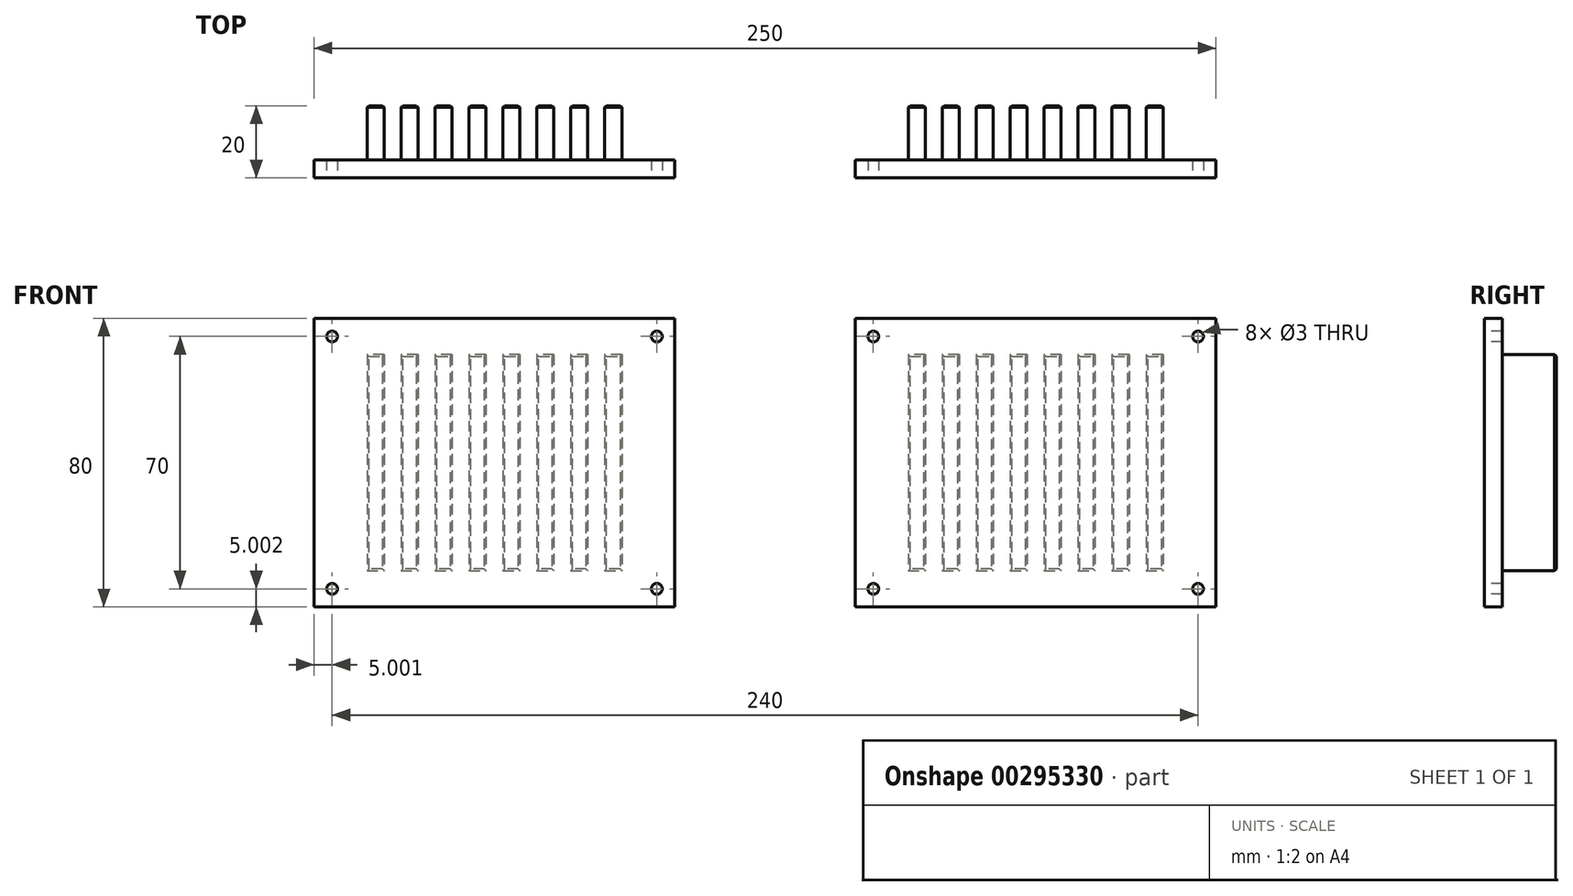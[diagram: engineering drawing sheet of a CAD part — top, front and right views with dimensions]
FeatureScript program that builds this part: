
annotation { "Feature Type Name" : "Feature", "Feature Type Description" : "" }
export const myFeature = defineFeature(function(context is Context, id is Id, definition is map)
    precondition{}
    {
        {
            var Q0;
            Q0=qCreatedBy(makeId("Front.planeOp"),FACE);
            var sketch = newSketch(context, id + "F0", { "sketchPlane" : qUnion([Q0])});
            skLineSegment(sketch, "E0.bottom", {"start": v(0.51, -38.35) * mm, "end": v(-79.49, -38.35) * mm});
            skLineSegment(sketch, "E0.top", {"start": v(0.51, 21.65) * mm, "end": v(-79.49, 21.65) * mm});
            skLineSegment(sketch, "E0.left", {"start": v(0.51, -38.35) * mm, "end": v(0.51, 21.65) * mm});
            skLineSegment(sketch, "E0.right", {"start": v(-79.49, -38.35) * mm, "end": v(-79.49, 21.65) * mm});
            skPoint(sketch, "E0.middle", {"position": v(-39.49, -8.35) * mm});
            skSolve(sketch);
        }
        {
            var Q0;
            Q0 = qSketchRegion(id + "F0", true);
            extrude(context, id + "F1", {"entities" : qUnion([Q0]), "oppositeDirection" : true, "depth" : 15 * mm, "offsetDistance" : 25 * mm});
        }
        {
            var Q0;
            Q0=makeQuery(id+"F1.opExtrude","CAP_FACE",FACE,{"disambiguationData":[OSD([sQuery(id+"F0.wireOp",EDGE,"E0.bottom"),sQuery(id+"F0.wireOp",EDGE,"E0.top"),sQuery(id+"F0.wireOp",EDGE,"E0.left"),sQuery(id+"F0.wireOp",EDGE,"E0.right")])],"isStart":true});
            var sketch = newSketch(context, id + "F2", { "sketchPlane" : qUnion([Q0])});
            skLineSegment(sketch, "E1", {"start": v(-79.49, 21.65) * mm, "end": v(0.51, -38.35) * mm, "construction": true});
            skLineSegment(sketch, "E2.bottom", {"start": v(10.51, -48.35) * mm, "end": v(-89.49, -48.35) * mm});
            skLineSegment(sketch, "E2.top", {"start": v(10.51, 31.65) * mm, "end": v(-89.49, 31.65) * mm});
            skLineSegment(sketch, "E2.left", {"start": v(10.51, -48.35) * mm, "end": v(10.51, 31.65) * mm});
            skLineSegment(sketch, "E2.right", {"start": v(-89.49, -48.35) * mm, "end": v(-89.49, 31.65) * mm});
            skPoint(sketch, "E2.middle", {"position": v(-39.49, -8.35) * mm});
            skSolve(sketch);
        }
        {
            var Q0;
            Q0 = qSketchRegion(id + "F2", true);
            extrude(context, id + "F3", {"entities" : qUnion([Q0]), "operationType" : NewBodyOperationType.ADD, "depth" : 5 * mm, "offsetDistance" : 25 * mm});
        }
        {
            var Q0;
            Q0=makeQuery(id+"F3.opExtrude","CAP_FACE",FACE,{"disambiguationData":[OSD([sQuery(id+"F2.wireOp",EDGE,"E2.bottom"),sQuery(id+"F2.wireOp",EDGE,"E2.top"),sQuery(id+"F2.wireOp",EDGE,"E2.left"),sQuery(id+"F2.wireOp",EDGE,"E2.right")])],"isStart":false});
            var sketch = newSketch(context, id + "F4", { "sketchPlane" : qUnion([Q0])});
            skLineSegment(sketch, "E3.bottom", {"start": v(-89.49, 31.65) * mm, "end": v(-84.49, 31.65) * mm, "construction": true});
            skLineSegment(sketch, "E3.top", {"start": v(-89.49, 26.65) * mm, "end": v(-84.49, 26.65) * mm, "construction": true});
            skLineSegment(sketch, "E3.left", {"start": v(-89.49, 31.65) * mm, "end": v(-89.49, 26.65) * mm, "construction": true});
            skLineSegment(sketch, "E3.right", {"start": v(-84.49, 31.65) * mm, "end": v(-84.49, 26.65) * mm, "construction": true});
            skCircle(sketch, "E4", {"center": v(-84.49, 26.65) * mm, "radius": 1.5 * mm});
            skLineSegment(sketch, "E5.bottom", {"start": v(-89.49, -48.35) * mm, "end": v(-84.49, -48.35) * mm, "construction": true});
            skLineSegment(sketch, "E5.top", {"start": v(-89.49, -43.35) * mm, "end": v(-84.49, -43.35) * mm, "construction": true});
            skLineSegment(sketch, "E5.left", {"start": v(-89.49, -48.35) * mm, "end": v(-89.49, -43.35) * mm, "construction": true});
            skLineSegment(sketch, "E5.right", {"start": v(-84.49, -48.35) * mm, "end": v(-84.49, -43.35) * mm, "construction": true});
            skLineSegment(sketch, "E6.bottom", {"start": v(10.51, -48.35) * mm, "end": v(5.51, -48.35) * mm, "construction": true});
            skLineSegment(sketch, "E6.top", {"start": v(10.51, -43.35) * mm, "end": v(5.51, -43.35) * mm, "construction": true});
            skLineSegment(sketch, "E6.left", {"start": v(10.51, -48.35) * mm, "end": v(10.51, -43.35) * mm, "construction": true});
            skLineSegment(sketch, "E6.right", {"start": v(5.51, -48.35) * mm, "end": v(5.51, -43.35) * mm, "construction": true});
            skLineSegment(sketch, "E7.bottom", {"start": v(10.51, 31.65) * mm, "end": v(5.51, 31.65) * mm, "construction": true});
            skLineSegment(sketch, "E7.top", {"start": v(10.51, 26.65) * mm, "end": v(5.51, 26.65) * mm, "construction": true});
            skLineSegment(sketch, "E7.left", {"start": v(10.51, 31.65) * mm, "end": v(10.51, 26.65) * mm, "construction": true});
            skLineSegment(sketch, "E7.right", {"start": v(5.51, 31.65) * mm, "end": v(5.51, 26.65) * mm, "construction": true});
            skCircle(sketch, "E8", {"center": v(5.51, 26.65) * mm, "radius": 1.5 * mm});
            skCircle(sketch, "E9", {"center": v(5.51, -43.35) * mm, "radius": 1.5 * mm});
            skCircle(sketch, "E10", {"center": v(-84.49, -43.35) * mm, "radius": 1.5 * mm});
            skLineSegment(sketch, "E11", {"start": v(-39.49, 31.65) * mm, "end": v(-39.49, -48.35) * mm, "construction": true});
            skPoint(sketch, "E12", {"position": v(-39.49, -8.35) * mm});
            skSolve(sketch);
        }
        {
            var Q0;
            Q0 = qSketchRegion(id + "F4", true);
            extrude(context, id + "F5", {"entities" : qUnion([Q0]), "operationType" : NewBodyOperationType.REMOVE, "oppositeDirection" : true, "depth" : 5 * mm, "offsetDistance" : 25 * mm});
        }
        {
            var Q0;
            Q0=makeQuery(id+"F1.opExtrude","CAP_FACE",FACE,{"disambiguationData":[OSD([sQuery(id+"F0.wireOp",EDGE,"E0.bottom"),sQuery(id+"F0.wireOp",EDGE,"E0.top"),sQuery(id+"F0.wireOp",EDGE,"E0.left"),sQuery(id+"F0.wireOp",EDGE,"E0.right")])],"isStart":false});
            var sketch = newSketch(context, id + "F6", { "sketchPlane" : qUnion([Q0])});
            skLineSegment(sketch, "E13.bottom", {"start": v(-0.51, 21.65) * mm, "end": v(4.2, 21.65) * mm});
            skLineSegment(sketch, "E13.top", {"start": v(-0.51, -38.35) * mm, "end": v(4.2, -38.35) * mm});
            skLineSegment(sketch, "E13.left", {"start": v(-0.51, 21.65) * mm, "end": v(-0.51, -38.35) * mm});
            skLineSegment(sketch, "E13.right", {"start": v(4.2, 21.65) * mm, "end": v(4.2, -38.35) * mm});
            skLineSegment(sketch, "E14.1.0.0", {"start": v(8.9, 21.65) * mm, "end": v(13.6, 21.65) * mm});
            skLineSegment(sketch, "E14.1.0.1", {"start": v(13.6, 21.65) * mm, "end": v(13.6, -38.35) * mm});
            skLineSegment(sketch, "E14.1.0.2", {"start": v(8.9, 21.65) * mm, "end": v(8.9, -38.35) * mm});
            skLineSegment(sketch, "E14.1.0.3", {"start": v(8.9, -38.35) * mm, "end": v(13.6, -38.35) * mm});
            skLineSegment(sketch, "E14.2.0.0", {"start": v(18.31, 21.65) * mm, "end": v(23.02, 21.65) * mm});
            skLineSegment(sketch, "E14.2.0.1", {"start": v(23.02, 21.65) * mm, "end": v(23.02, -38.35) * mm});
            skLineSegment(sketch, "E14.2.0.2", {"start": v(18.31, 21.65) * mm, "end": v(18.31, -38.35) * mm});
            skLineSegment(sketch, "E14.2.0.3", {"start": v(18.31, -38.35) * mm, "end": v(23.02, -38.35) * mm});
            skLineSegment(sketch, "E14.3.0.0", {"start": v(27.72, 21.65) * mm, "end": v(32.43, 21.65) * mm});
            skLineSegment(sketch, "E14.3.0.1", {"start": v(32.43, 21.65) * mm, "end": v(32.43, -38.35) * mm});
            skLineSegment(sketch, "E14.3.0.2", {"start": v(27.72, 21.65) * mm, "end": v(27.72, -38.35) * mm});
            skLineSegment(sketch, "E14.3.0.3", {"start": v(27.72, -38.35) * mm, "end": v(32.43, -38.35) * mm});
            skLineSegment(sketch, "E14.4.0.0", {"start": v(37.14, 21.65) * mm, "end": v(41.84, 21.65) * mm});
            skLineSegment(sketch, "E14.4.0.1", {"start": v(41.84, 21.65) * mm, "end": v(41.84, -38.35) * mm});
            skLineSegment(sketch, "E14.4.0.2", {"start": v(37.14, 21.65) * mm, "end": v(37.14, -38.35) * mm});
            skLineSegment(sketch, "E14.4.0.3", {"start": v(37.14, -38.35) * mm, "end": v(41.84, -38.35) * mm});
            skLineSegment(sketch, "E14.5.0.0", {"start": v(46.55, 21.65) * mm, "end": v(51.25, 21.65) * mm});
            skLineSegment(sketch, "E14.5.0.1", {"start": v(51.25, 21.65) * mm, "end": v(51.25, -38.35) * mm});
            skLineSegment(sketch, "E14.5.0.2", {"start": v(46.55, 21.65) * mm, "end": v(46.55, -38.35) * mm});
            skLineSegment(sketch, "E14.5.0.3", {"start": v(46.55, -38.35) * mm, "end": v(51.25, -38.35) * mm});
            skLineSegment(sketch, "E14.6.0.0", {"start": v(55.96, 21.65) * mm, "end": v(60.67, 21.65) * mm});
            skLineSegment(sketch, "E14.6.0.1", {"start": v(60.67, 21.65) * mm, "end": v(60.67, -38.35) * mm});
            skLineSegment(sketch, "E14.6.0.2", {"start": v(55.96, 21.65) * mm, "end": v(55.96, -38.35) * mm});
            skLineSegment(sketch, "E14.6.0.3", {"start": v(55.96, -38.35) * mm, "end": v(60.67, -38.35) * mm});
            skLineSegment(sketch, "E14.7.0.0", {"start": v(65.37, 21.65) * mm, "end": v(70.08, 21.65) * mm});
            skLineSegment(sketch, "E14.7.0.1", {"start": v(70.08, 21.65) * mm, "end": v(70.08, -38.35) * mm});
            skLineSegment(sketch, "E14.7.0.2", {"start": v(65.37, 21.65) * mm, "end": v(65.37, -38.35) * mm});
            skLineSegment(sketch, "E14.7.0.3", {"start": v(65.37, -38.35) * mm, "end": v(70.08, -38.35) * mm});
            skLineSegment(sketch, "E14.8.0.0", {"start": v(74.78, 21.65) * mm, "end": v(79.5, 21.65) * mm});
            skLineSegment(sketch, "E14.8.0.1", {"start": v(79.5, 21.65) * mm, "end": v(79.5, -38.35) * mm});
            skLineSegment(sketch, "E14.8.0.2", {"start": v(74.78, 21.65) * mm, "end": v(74.78, -38.35) * mm});
            skLineSegment(sketch, "E14.8.0.3", {"start": v(74.78, -38.35) * mm, "end": v(79.5, -38.35) * mm});
            skLineSegment(sketch, "E14.direction1", {"start": v(-0.51, 21.65) * mm, "end": v(8.9, 21.65) * mm, "construction": true});
            skSolve(sketch);
        }
        {
            var Q0;
            Q0=makeQuery(id+"F6.imprint","IMPRINT",FACE,{"disambiguationData":[TD([[makeQuery(id+"F6.imprint","IMPRINT",EDGE,{"derivedFrom":sQuery(id+"F6.wireOp",EDGE,"E13.bottom")}),-1.0]])]});
            var Q1;
            Q1=makeQuery(id+"F6.imprint","IMPRINT",FACE,{"disambiguationData":[TD([[makeQuery(id+"F6.imprint","IMPRINT",EDGE,{"derivedFrom":sQuery(id+"F6.wireOp",EDGE,"E14.1.0.0")}),-1.0]])]});
            var Q2;
            Q2=makeQuery(id+"F6.imprint","IMPRINT",FACE,{"disambiguationData":[TD([[makeQuery(id+"F6.imprint","IMPRINT",EDGE,{"derivedFrom":sQuery(id+"F6.wireOp",EDGE,"E14.2.0.0")}),-1.0]])]});
            var Q3;
            Q3=makeQuery(id+"F6.imprint","IMPRINT",FACE,{"disambiguationData":[TD([[makeQuery(id+"F6.imprint","IMPRINT",EDGE,{"derivedFrom":sQuery(id+"F6.wireOp",EDGE,"E14.3.0.0")}),-1.0]])]});
            var Q4;
            Q4=makeQuery(id+"F6.imprint","IMPRINT",FACE,{"disambiguationData":[TD([[makeQuery(id+"F6.imprint","IMPRINT",EDGE,{"derivedFrom":sQuery(id+"F6.wireOp",EDGE,"E14.4.0.0")}),-1.0]])]});
            var Q5;
            Q5=makeQuery(id+"F6.imprint","IMPRINT",FACE,{"disambiguationData":[TD([[makeQuery(id+"F6.imprint","IMPRINT",EDGE,{"derivedFrom":sQuery(id+"F6.wireOp",EDGE,"E14.5.0.0")}),-1.0]])]});
            var Q6;
            Q6=makeQuery(id+"F6.imprint","IMPRINT",FACE,{"disambiguationData":[TD([[makeQuery(id+"F6.imprint","IMPRINT",EDGE,{"derivedFrom":sQuery(id+"F6.wireOp",EDGE,"E14.6.0.0")}),-1.0]])]});
            var Q7;
            Q7=makeQuery(id+"F6.imprint","IMPRINT",FACE,{"disambiguationData":[TD([[makeQuery(id+"F6.imprint","IMPRINT",EDGE,{"derivedFrom":sQuery(id+"F6.wireOp",EDGE,"E14.7.0.0")}),-1.0]])]});
            var Q8;
            {var subQ2=sQuery(id+"F6.wireOp",EDGE,"E14.8.0.2");Q8=makeQuery(id+"F6.imprint","IMPRINT",FACE,{"disambiguationData":[TD([[makeQuery(id+"F6.imprint","IMPRINT",EDGE,{"derivedFrom":subQ2}),1.0]])]});}
            extrude(context, id + "F7", {"entities" : qUnion([Q0, Q1, Q2, Q3, Q4, Q5, Q6, Q7, Q8]), "operationType" : NewBodyOperationType.REMOVE, "oppositeDirection" : true, "depth" : 15 * mm, "offsetDistance" : 25 * mm});
        }
        {
            var Q0;
            Q0=makeQuery(id+"F7.boolean.opBoolean","COPY",EDGE,{"derivedFrom":makeQuery(id+"F7.opExtrude","CAP_EDGE",EDGE,{"disambiguationData":[OSD([sQuery(id+"F6.wireOp",EDGE,"E14.7.0.1")])],"isStart":true})});
            var Q1;
            {var subQ0=sQuery(id+"F0.wireOp",EDGE,"E0.bottom");var subQ1=sQuery(id+"F0.wireOp",EDGE,"E0.top");Q1=makeQuery(id+"F7.boolean.opBoolean","SPLIT",FACE,{"disambiguationData":[TD([makeQuery(id+"F7.opExtrude","SWEPT_FACE",FACE,{"disambiguationData":[OSD([sQuery(id+"F6.wireOp",EDGE,"E14.1.0.1")])]})])],"derivedFrom":makeQuery(id+"F1.opExtrude","CAP_FACE",FACE,{"disambiguationData":[OSD([subQ0,subQ1,sQuery(id+"F0.wireOp",EDGE,"E0.left"),sQuery(id+"F0.wireOp",EDGE,"E0.right")])],"isStart":false})});}
            var Q2;
            {var subQ0=sQuery(id+"F0.wireOp",EDGE,"E0.bottom");var subQ1=sQuery(id+"F0.wireOp",EDGE,"E0.top");Q2=makeQuery(id+"F7.boolean.opBoolean","SPLIT",FACE,{"disambiguationData":[TD([makeQuery(id+"F7.opExtrude","SWEPT_FACE",FACE,{"disambiguationData":[OSD([sQuery(id+"F6.wireOp",EDGE,"E14.2.0.1")])]})])],"derivedFrom":makeQuery(id+"F1.opExtrude","CAP_FACE",FACE,{"disambiguationData":[OSD([subQ0,subQ1,sQuery(id+"F0.wireOp",EDGE,"E0.left"),sQuery(id+"F0.wireOp",EDGE,"E0.right")])],"isStart":false})});}
            var Q3;
            {var subQ0=sQuery(id+"F0.wireOp",EDGE,"E0.top");Q3=makeQuery(id+"F7.boolean.opBoolean","SPLIT",EDGE,{"disambiguationData":[TD([makeQuery(id+"F7.opExtrude","SWEPT_FACE",FACE,{"disambiguationData":[OSD([sQuery(id+"F6.wireOp",EDGE,"E14.2.0.1")])]})])],"derivedFrom":makeQuery(id+"F1.opExtrude","CAP_EDGE",EDGE,{"disambiguationData":[OSD([subQ0])],"isStart":false})});}
            var Q4;
            Q4=makeQuery(id+"F7.boolean.opBoolean","COPY",EDGE,{"derivedFrom":makeQuery(id+"F7.opExtrude","CAP_EDGE",EDGE,{"disambiguationData":[OSD([sQuery(id+"F6.wireOp",EDGE,"E14.3.0.1")])],"isStart":true})});
            var Q5;
            Q5=makeQuery(id+"F7.boolean.opBoolean","COPY",EDGE,{"derivedFrom":makeQuery(id+"F7.opExtrude","CAP_EDGE",EDGE,{"disambiguationData":[OSD([sQuery(id+"F6.wireOp",EDGE,"E14.2.0.1")])],"isStart":true})});
            var Q6;
            Q6=makeQuery(id+"F7.boolean.opBoolean","COPY",EDGE,{"derivedFrom":makeQuery(id+"F7.opExtrude","CAP_EDGE",EDGE,{"disambiguationData":[OSD([sQuery(id+"F6.wireOp",EDGE,"E14.1.0.2")])],"isStart":true})});
            var Q7;
            Q7=makeQuery(id+"F7.boolean.opBoolean","COPY",EDGE,{"derivedFrom":makeQuery(id+"F7.opExtrude","CAP_EDGE",EDGE,{"disambiguationData":[OSD([sQuery(id+"F6.wireOp",EDGE,"E14.6.0.1")])],"isStart":true})});
            var Q8;
            Q8=makeQuery(id+"F7.boolean.opBoolean","COPY",EDGE,{"derivedFrom":makeQuery(id+"F7.opExtrude","CAP_EDGE",EDGE,{"disambiguationData":[OSD([sQuery(id+"F6.wireOp",EDGE,"E13.right")])],"isStart":true})});
            var Q9;
            Q9=makeQuery(id+"F7.boolean.opBoolean","COPY",EDGE,{"derivedFrom":makeQuery(id+"F7.opExtrude","CAP_EDGE",EDGE,{"disambiguationData":[OSD([sQuery(id+"F6.wireOp",EDGE,"E14.3.0.2")])],"isStart":true})});
            var Q10;
            {var subQ0=sQuery(id+"F0.wireOp",EDGE,"E0.bottom");var subQ1=sQuery(id+"F0.wireOp",EDGE,"E0.top");Q10=makeQuery(id+"F7.boolean.opBoolean","SPLIT",FACE,{"disambiguationData":[TD([makeQuery(id+"F7.opExtrude","SWEPT_FACE",FACE,{"disambiguationData":[OSD([sQuery(id+"F6.wireOp",EDGE,"E14.3.0.1")])]})])],"derivedFrom":makeQuery(id+"F1.opExtrude","CAP_FACE",FACE,{"disambiguationData":[OSD([subQ0,subQ1,sQuery(id+"F0.wireOp",EDGE,"E0.left"),sQuery(id+"F0.wireOp",EDGE,"E0.right")])],"isStart":false})});}
            var Q11;
            Q11=makeQuery(id+"F7.boolean.opBoolean","COPY",EDGE,{"derivedFrom":makeQuery(id+"F7.opExtrude","CAP_EDGE",EDGE,{"disambiguationData":[OSD([sQuery(id+"F6.wireOp",EDGE,"E14.7.0.2")])],"isStart":true})});
            var Q12;
            Q12=makeQuery(id+"F7.boolean.opBoolean","COPY",EDGE,{"derivedFrom":makeQuery(id+"F7.opExtrude","CAP_EDGE",EDGE,{"disambiguationData":[OSD([sQuery(id+"F6.wireOp",EDGE,"E14.6.0.2")])],"isStart":true})});
            var Q13;
            {var subQ0=sQuery(id+"F0.wireOp",EDGE,"E0.bottom");var subQ1=sQuery(id+"F0.wireOp",EDGE,"E0.top");Q13=makeQuery(id+"F7.boolean.opBoolean","SPLIT",FACE,{"disambiguationData":[TD([makeQuery(id+"F7.opExtrude","SWEPT_FACE",FACE,{"disambiguationData":[OSD([sQuery(id+"F6.wireOp",EDGE,"E14.4.0.1")])]})])],"derivedFrom":makeQuery(id+"F1.opExtrude","CAP_FACE",FACE,{"disambiguationData":[OSD([subQ0,subQ1,sQuery(id+"F0.wireOp",EDGE,"E0.left"),sQuery(id+"F0.wireOp",EDGE,"E0.right")])],"isStart":false})});}
            var Q14;
            {var subQ0=sQuery(id+"F0.wireOp",EDGE,"E0.bottom");var subQ1=sQuery(id+"F0.wireOp",EDGE,"E0.top");Q14=makeQuery(id+"F7.boolean.opBoolean","SPLIT",FACE,{"disambiguationData":[TD([makeQuery(id+"F7.opExtrude","SWEPT_FACE",FACE,{"disambiguationData":[OSD([sQuery(id+"F6.wireOp",EDGE,"E14.6.0.1")])]})])],"derivedFrom":makeQuery(id+"F1.opExtrude","CAP_FACE",FACE,{"disambiguationData":[OSD([subQ0,subQ1,sQuery(id+"F0.wireOp",EDGE,"E0.left"),sQuery(id+"F0.wireOp",EDGE,"E0.right")])],"isStart":false})});}
            var Q15;
            {var subQ0=sQuery(id+"F0.wireOp",EDGE,"E0.bottom");var subQ1=sQuery(id+"F0.wireOp",EDGE,"E0.top");Q15=makeQuery(id+"F7.boolean.opBoolean","SPLIT",FACE,{"disambiguationData":[TD([makeQuery(id+"F7.opExtrude","SWEPT_FACE",FACE,{"disambiguationData":[OSD([sQuery(id+"F6.wireOp",EDGE,"E14.5.0.1")])]})])],"derivedFrom":makeQuery(id+"F1.opExtrude","CAP_FACE",FACE,{"disambiguationData":[OSD([subQ0,subQ1,sQuery(id+"F0.wireOp",EDGE,"E0.left"),sQuery(id+"F0.wireOp",EDGE,"E0.right")])],"isStart":false})});}
            var Q16;
            Q16=makeQuery(id+"F7.boolean.opBoolean","COPY",EDGE,{"derivedFrom":makeQuery(id+"F7.opExtrude","CAP_EDGE",EDGE,{"disambiguationData":[OSD([sQuery(id+"F6.wireOp",EDGE,"E14.5.0.1")])],"isStart":true})});
            var Q17;
            Q17=makeQuery(id+"F7.boolean.opBoolean","COPY",EDGE,{"derivedFrom":makeQuery(id+"F7.opExtrude","CAP_EDGE",EDGE,{"disambiguationData":[OSD([sQuery(id+"F6.wireOp",EDGE,"E14.4.0.2")])],"isStart":true})});
            var Q18;
            {var subQ0=sQuery(id+"F0.wireOp",EDGE,"E0.bottom");var subQ1=sQuery(id+"F0.wireOp",EDGE,"E0.top");Q18=makeQuery(id+"F7.boolean.opBoolean","SPLIT",FACE,{"disambiguationData":[TD([makeQuery(id+"F7.opExtrude","SWEPT_FACE",FACE,{"disambiguationData":[OSD([sQuery(id+"F6.wireOp",EDGE,"E13.right")])]})])],"derivedFrom":makeQuery(id+"F1.opExtrude","CAP_FACE",FACE,{"disambiguationData":[OSD([subQ0,subQ1,sQuery(id+"F0.wireOp",EDGE,"E0.left"),sQuery(id+"F0.wireOp",EDGE,"E0.right")])],"isStart":false})});}
            var Q19;
            Q19=makeQuery(id+"F7.boolean.opBoolean","COPY",EDGE,{"derivedFrom":makeQuery(id+"F7.opExtrude","CAP_EDGE",EDGE,{"disambiguationData":[OSD([sQuery(id+"F6.wireOp",EDGE,"E14.4.0.1")])],"isStart":true})});
            var Q20;
            Q20=makeQuery(id+"F7.boolean.opBoolean","COPY",EDGE,{"derivedFrom":makeQuery(id+"F7.opExtrude","CAP_EDGE",EDGE,{"disambiguationData":[OSD([sQuery(id+"F6.wireOp",EDGE,"E14.8.0.2")])],"isStart":true})});
            var Q21;
            {var subQ0=sQuery(id+"F0.wireOp",EDGE,"E0.bottom");var subQ1=sQuery(id+"F0.wireOp",EDGE,"E0.top");Q21=makeQuery(id+"F7.boolean.opBoolean","SPLIT",FACE,{"disambiguationData":[TD([makeQuery(id+"F7.opExtrude","SWEPT_FACE",FACE,{"disambiguationData":[OSD([sQuery(id+"F6.wireOp",EDGE,"E14.7.0.1")])]})])],"derivedFrom":makeQuery(id+"F1.opExtrude","CAP_FACE",FACE,{"disambiguationData":[OSD([subQ0,subQ1,sQuery(id+"F0.wireOp",EDGE,"E0.left"),sQuery(id+"F0.wireOp",EDGE,"E0.right")])],"isStart":false})});}
            var Q22;
            Q22=makeQuery(id+"F7.boolean.opBoolean","COPY",EDGE,{"derivedFrom":makeQuery(id+"F7.opExtrude","CAP_EDGE",EDGE,{"disambiguationData":[OSD([sQuery(id+"F6.wireOp",EDGE,"E14.2.0.2")])],"isStart":true})});
            var Q23;
            Q23=makeQuery(id+"F7.boolean.opBoolean","COPY",EDGE,{"derivedFrom":makeQuery(id+"F7.opExtrude","CAP_EDGE",EDGE,{"disambiguationData":[OSD([sQuery(id+"F6.wireOp",EDGE,"E14.1.0.1")])],"isStart":true})});
            var Q24;
            {var subQ0=sQuery(id+"F0.wireOp",EDGE,"E0.top");Q24=makeQuery(id+"F7.boolean.opBoolean","SPLIT",EDGE,{"disambiguationData":[TD([makeQuery(id+"F7.opExtrude","SWEPT_FACE",FACE,{"disambiguationData":[OSD([sQuery(id+"F6.wireOp",EDGE,"E14.3.0.1")])]})])],"derivedFrom":makeQuery(id+"F1.opExtrude","CAP_EDGE",EDGE,{"disambiguationData":[OSD([subQ0])],"isStart":false})});}
            var Q25;
            {var subQ0=sQuery(id+"F0.wireOp",EDGE,"E0.bottom");Q25=makeQuery(id+"F7.boolean.opBoolean","SPLIT",EDGE,{"disambiguationData":[TD([makeQuery(id+"F7.opExtrude","SWEPT_FACE",FACE,{"disambiguationData":[OSD([sQuery(id+"F6.wireOp",EDGE,"E14.4.0.1")])]})])],"derivedFrom":makeQuery(id+"F1.opExtrude","CAP_EDGE",EDGE,{"disambiguationData":[OSD([subQ0])],"isStart":false})});}
            var Q26;
            {var subQ0=sQuery(id+"F0.wireOp",EDGE,"E0.top");Q26=makeQuery(id+"F7.boolean.opBoolean","SPLIT",EDGE,{"disambiguationData":[TD([makeQuery(id+"F7.opExtrude","SWEPT_FACE",FACE,{"disambiguationData":[OSD([sQuery(id+"F6.wireOp",EDGE,"E14.4.0.1")])]})])],"derivedFrom":makeQuery(id+"F1.opExtrude","CAP_EDGE",EDGE,{"disambiguationData":[OSD([subQ0])],"isStart":false})});}
            var Q27;
            {var subQ0=sQuery(id+"F0.wireOp",EDGE,"E0.top");Q27=makeQuery(id+"F7.boolean.opBoolean","SPLIT",EDGE,{"disambiguationData":[TD([makeQuery(id+"F7.opExtrude","SWEPT_FACE",FACE,{"disambiguationData":[OSD([sQuery(id+"F6.wireOp",EDGE,"E14.1.0.1")])]})])],"derivedFrom":makeQuery(id+"F1.opExtrude","CAP_EDGE",EDGE,{"disambiguationData":[OSD([subQ0])],"isStart":false})});}
            var Q28;
            {var subQ0=sQuery(id+"F0.wireOp",EDGE,"E0.bottom");Q28=makeQuery(id+"F7.boolean.opBoolean","SPLIT",EDGE,{"disambiguationData":[TD([makeQuery(id+"F7.opExtrude","SWEPT_FACE",FACE,{"disambiguationData":[OSD([sQuery(id+"F6.wireOp",EDGE,"E14.6.0.1")])]})])],"derivedFrom":makeQuery(id+"F1.opExtrude","CAP_EDGE",EDGE,{"disambiguationData":[OSD([subQ0])],"isStart":false})});}
            var Q29;
            Q29=makeQuery(id+"F7.boolean.opBoolean","COPY",EDGE,{"derivedFrom":makeQuery(id+"F7.opExtrude","CAP_EDGE",EDGE,{"disambiguationData":[OSD([sQuery(id+"F6.wireOp",EDGE,"E14.5.0.2")])],"isStart":true})});
            var Q30;
            {var subQ0=sQuery(id+"F0.wireOp",EDGE,"E0.bottom");Q30=makeQuery(id+"F7.boolean.opBoolean","SPLIT",EDGE,{"disambiguationData":[TD([makeQuery(id+"F7.opExtrude","SWEPT_FACE",FACE,{"disambiguationData":[OSD([sQuery(id+"F6.wireOp",EDGE,"E14.3.0.1")])]})])],"derivedFrom":makeQuery(id+"F1.opExtrude","CAP_EDGE",EDGE,{"disambiguationData":[OSD([subQ0])],"isStart":false})});}
            var Q31;
            {var subQ0=sQuery(id+"F0.wireOp",EDGE,"E0.bottom");Q31=makeQuery(id+"F7.boolean.opBoolean","SPLIT",EDGE,{"disambiguationData":[TD([makeQuery(id+"F7.opExtrude","SWEPT_FACE",FACE,{"disambiguationData":[OSD([sQuery(id+"F6.wireOp",EDGE,"E14.1.0.1")])]})])],"derivedFrom":makeQuery(id+"F1.opExtrude","CAP_EDGE",EDGE,{"disambiguationData":[OSD([subQ0])],"isStart":false})});}
            var Q32;
            {var subQ0=sQuery(id+"F0.wireOp",EDGE,"E0.top");Q32=makeQuery(id+"F7.boolean.opBoolean","SPLIT",EDGE,{"disambiguationData":[TD([makeQuery(id+"F7.opExtrude","SWEPT_FACE",FACE,{"disambiguationData":[OSD([sQuery(id+"F6.wireOp",EDGE,"E14.7.0.1")])]})])],"derivedFrom":makeQuery(id+"F1.opExtrude","CAP_EDGE",EDGE,{"disambiguationData":[OSD([subQ0])],"isStart":false})});}
            var Q33;
            {var subQ0=sQuery(id+"F0.wireOp",EDGE,"E0.bottom");Q33=makeQuery(id+"F7.boolean.opBoolean","SPLIT",EDGE,{"disambiguationData":[TD([makeQuery(id+"F7.opExtrude","SWEPT_FACE",FACE,{"disambiguationData":[OSD([sQuery(id+"F6.wireOp",EDGE,"E14.7.0.1")])]})])],"derivedFrom":makeQuery(id+"F1.opExtrude","CAP_EDGE",EDGE,{"disambiguationData":[OSD([subQ0])],"isStart":false})});}
            var Q34;
            {var subQ0=sQuery(id+"F0.wireOp",EDGE,"E0.top");Q34=makeQuery(id+"F7.boolean.opBoolean","SPLIT",EDGE,{"disambiguationData":[TD([makeQuery(id+"F7.opExtrude","SWEPT_FACE",FACE,{"disambiguationData":[OSD([sQuery(id+"F6.wireOp",EDGE,"E14.5.0.1")])]})])],"derivedFrom":makeQuery(id+"F1.opExtrude","CAP_EDGE",EDGE,{"disambiguationData":[OSD([subQ0])],"isStart":false})});}
            var Q35;
            {var subQ0=sQuery(id+"F0.wireOp",EDGE,"E0.top");Q35=makeQuery(id+"F7.boolean.opBoolean","SPLIT",EDGE,{"disambiguationData":[TD([makeQuery(id+"F7.opExtrude","SWEPT_FACE",FACE,{"disambiguationData":[OSD([sQuery(id+"F6.wireOp",EDGE,"E14.6.0.1")])]})])],"derivedFrom":makeQuery(id+"F1.opExtrude","CAP_EDGE",EDGE,{"disambiguationData":[OSD([subQ0])],"isStart":false})});}
            var Q36;
            {var subQ0=sQuery(id+"F0.wireOp",EDGE,"E0.bottom");Q36=makeQuery(id+"F7.boolean.opBoolean","SPLIT",EDGE,{"disambiguationData":[TD([makeQuery(id+"F7.opExtrude","SWEPT_FACE",FACE,{"disambiguationData":[OSD([sQuery(id+"F6.wireOp",EDGE,"E14.2.0.1")])]})])],"derivedFrom":makeQuery(id+"F1.opExtrude","CAP_EDGE",EDGE,{"disambiguationData":[OSD([subQ0])],"isStart":false})});}
            var Q37;
            {var subQ0=sQuery(id+"F0.wireOp",EDGE,"E0.top");Q37=makeQuery(id+"F7.boolean.opBoolean","SPLIT",EDGE,{"disambiguationData":[TD([makeQuery(id+"F7.opExtrude","SWEPT_FACE",FACE,{"disambiguationData":[OSD([sQuery(id+"F6.wireOp",EDGE,"E13.right")])]})])],"derivedFrom":makeQuery(id+"F1.opExtrude","CAP_EDGE",EDGE,{"disambiguationData":[OSD([subQ0])],"isStart":false})});}
            var Q38;
            {var subQ0=sQuery(id+"F0.wireOp",EDGE,"E0.bottom");Q38=makeQuery(id+"F7.boolean.opBoolean","SPLIT",EDGE,{"disambiguationData":[TD([makeQuery(id+"F7.opExtrude","SWEPT_FACE",FACE,{"disambiguationData":[OSD([sQuery(id+"F6.wireOp",EDGE,"E13.right")])]})])],"derivedFrom":makeQuery(id+"F1.opExtrude","CAP_EDGE",EDGE,{"disambiguationData":[OSD([subQ0])],"isStart":false})});}
            var Q39;
            {var subQ0=sQuery(id+"F0.wireOp",EDGE,"E0.bottom");Q39=makeQuery(id+"F7.boolean.opBoolean","SPLIT",EDGE,{"disambiguationData":[TD([makeQuery(id+"F7.opExtrude","SWEPT_FACE",FACE,{"disambiguationData":[OSD([sQuery(id+"F6.wireOp",EDGE,"E14.5.0.1")])]})])],"derivedFrom":makeQuery(id+"F1.opExtrude","CAP_EDGE",EDGE,{"disambiguationData":[OSD([subQ0])],"isStart":false})});}
            chamfer(context, id + "F8", {"entities" : qUnion([Q0, Q1, Q2, Q3, Q4, Q5, Q6, Q7, Q8, Q9, Q10, Q11, Q12, Q13, Q14, Q15, Q16, Q17, Q18, Q19, Q20, Q21, Q22, Q23, Q24, Q25, Q26, Q27, Q28, Q29, Q30, Q31, Q32, Q33, Q34, Q35, Q36, Q37, Q38, Q39]), "width" : 0.5 * mm, "tangentPropagation" : true});
        }
        {
            var Q0;
            Q0=makeQuery(id+"F1.opExtrude","SWEPT_BODY",BODY,{"disambiguationData":[OSD([sQuery(id+"F0.wireOp",EDGE,"E0.bottom"),sQuery(id+"F0.wireOp",EDGE,"E0.top"),sQuery(id+"F0.wireOp",EDGE,"E0.left"),sQuery(id+"F0.wireOp",EDGE,"E0.right")])]});
            transform(context, id + "F9", {"entities" : qUnion([Q0]), "transformType" : TransformType.TRANSLATION_3D, "dx" : 150 * mm, "dy" : 0 * mm, "dz" : 0 * mm, "makeCopy" : true});
        }
    });
